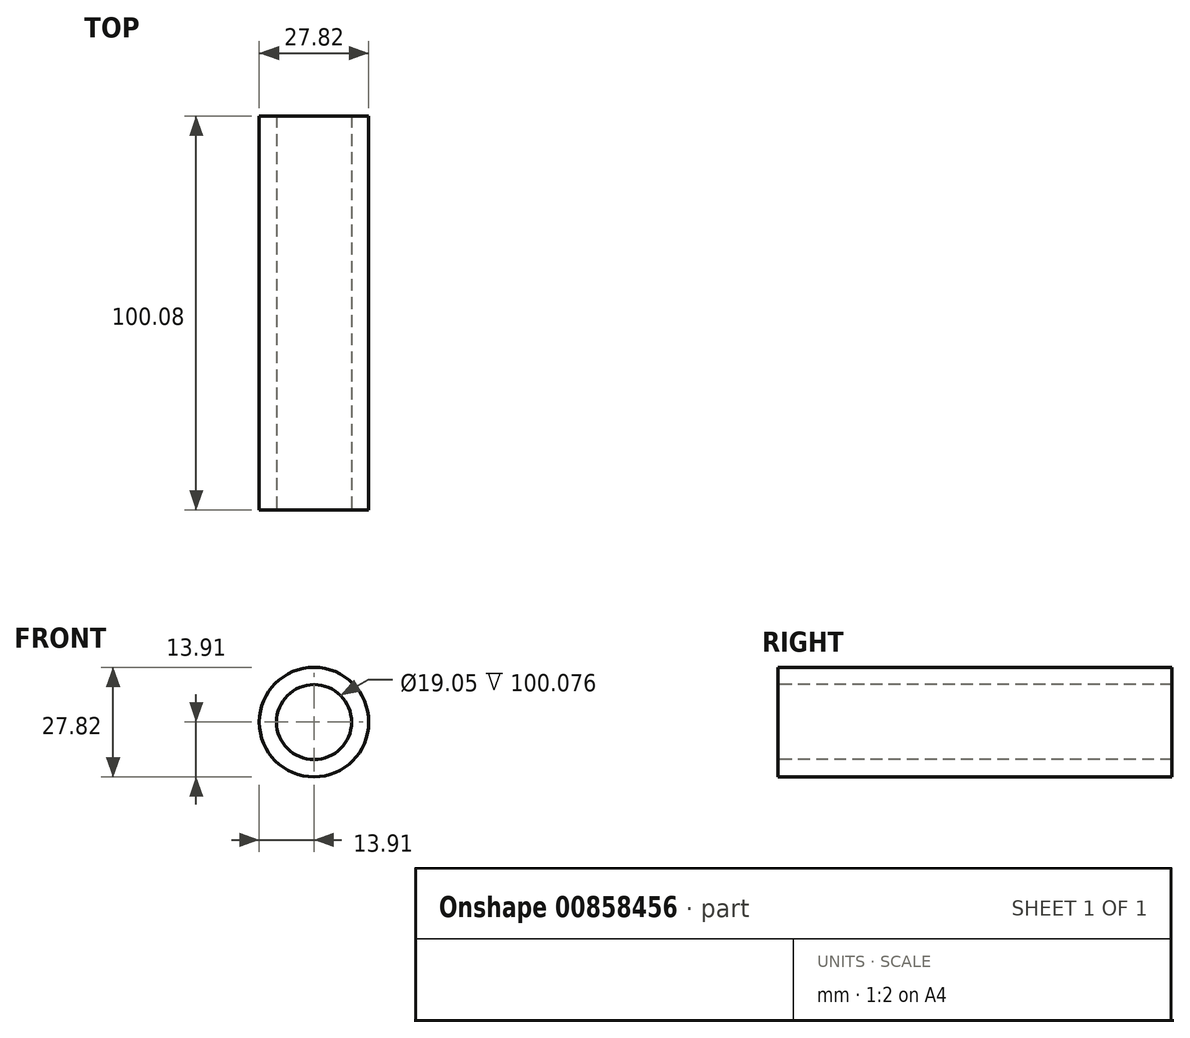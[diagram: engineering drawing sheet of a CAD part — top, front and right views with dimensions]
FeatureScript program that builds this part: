
annotation { "Feature Type Name" : "Feature", "Feature Type Description" : "" }
export const myFeature = defineFeature(function(context is Context, id is Id, definition is map)
    precondition{}
    {
        {
            var Q0;
            Q0=qCreatedBy(makeId("Front.planeOp"),FACE);
            var sketch = newSketch(context, id + "F0", { "sketchPlane" : qUnion([Q0])});
            skCircle(sketch, "E0", {"center": v(0, 0) * mm, "radius": 13.91 * mm});
            skSolve(sketch);
        }
        {
            var Q0;
            Q0=makeQuery(id+"F0.imprint","IMPRINT",FACE,{"disambiguationData":[TD([[makeQuery(id+"F0.imprint","IMPRINT",EDGE,{"derivedFrom":sQuery(id+"F0.wireOp",EDGE,"E0")}),1.0]])]});
            extrude(context, id + "F1", {"entities" : qUnion([Q0]), "endBound" : BoundingType.SYMMETRIC, "depth" : 100.08 * mm, "offsetDistance" : 25.4 * mm});
        }
        {
            var Q0;
            Q0=makeQuery(id+"F1.opExtrude","CAP_FACE",FACE,{"disambiguationData":[OSD([sQuery(id+"F0.wireOp",EDGE,"E0")])],"isStart":false});
            var sketch = newSketch(context, id + "F2", { "sketchPlane" : qUnion([Q0])});
            skPoint(sketch, "E1", {"position": v(0, 0) * mm});
            skPoint(sketch, "E2", {"position": v(-145.13, 14.07) * mm});
            skSolve(sketch);
        }
        {
            var Q0;
            Q0=sQuery(id+"F2.wireOp",VERTEX,"E1");
            var Q1;
            Q1=sQuery(id+"F2.wireOp",VERTEX,"E2");
            var Q2;
            Q2=makeQuery(id+"F1.opExtrude","SWEPT_BODY",BODY,{"disambiguationData":[OSD([sQuery(id+"F0.wireOp",EDGE,"E0")])]});
            hole(context, id + "F3", {"style" : HoleStyle.SIMPLE, "endStyle" : HoleEndStyle.THROUGH, "holeDiameter" : 19.05 * mm, "majorDiameter" : 6.35 * mm, "isTappedThrough" : true, "tappedDepth" : 12.7 * mm, "tapClearance" : 3, "locations" : qUnion([Q0, Q1]), "scope" : qUnion([Q2])});
        }
    });
